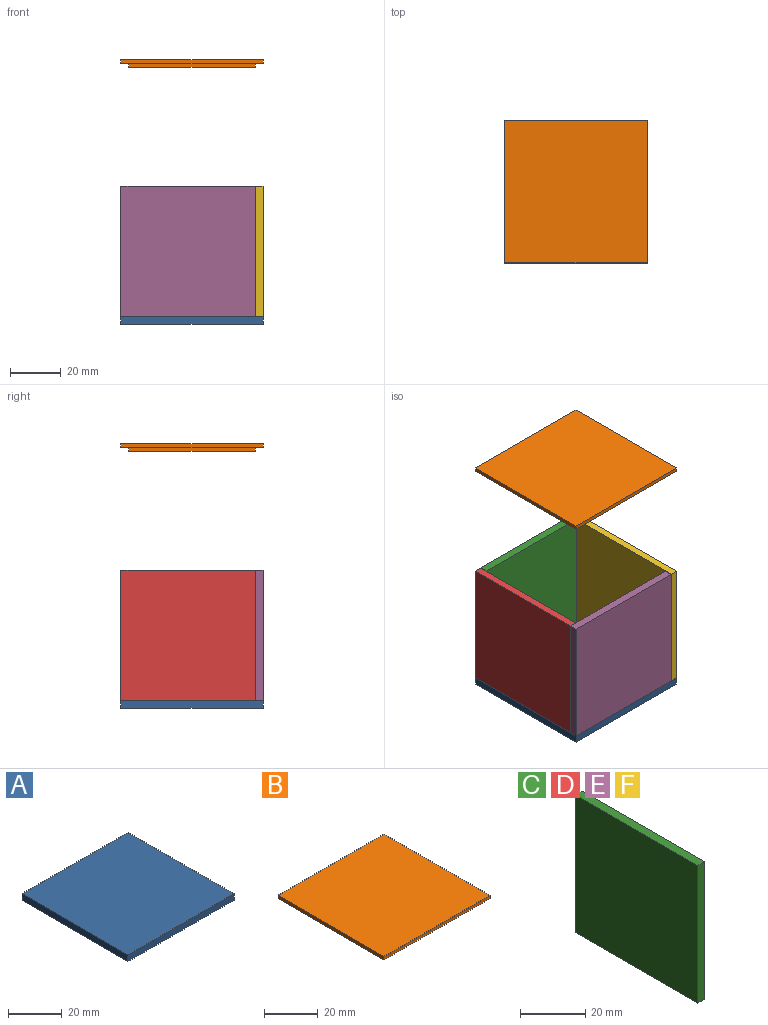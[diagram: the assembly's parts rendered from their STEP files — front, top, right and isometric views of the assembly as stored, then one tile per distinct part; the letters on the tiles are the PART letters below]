
ASSEMBLY  parts=6 mates=14
PART A: 6 faces, bbox 56x56x3 mm
  f0: plane 56x3mm, normal (0,1,0), area 168mm2, adj f1,f3,f4,f5
  f1: plane 56x3mm, normal (-1,0,0), area 168mm2, adj f0,f2,f4,f5
  f2: plane 56x3mm, normal (0,-1,0), area 168mm2, adj f1,f3,f4,f5
  f3: plane 56x3mm, normal (1,0,0), area 168mm2, adj f0,f2,f4,f5
  f4: plane 56x56mm, normal (0,0,1), area 3136mm2, adj f0,f1,f2,f3
  f5: plane 56x56mm, normal (0,0,-1), area 3136mm2, adj f0,f1,f2,f3
PART B: 11 faces, bbox 56x56x3 mm
  f0: plane 56x1.5mm, normal (0,1,0), area 84mm2, adj f1,f3,f4,f9
  f1: plane 56x1.5mm, normal (-1,0,0), area 84mm2, adj f0,f2,f4,f9
  f2: plane 56x1.5mm, normal (0,-1,0), area 84mm2, adj f1,f3,f4,f9
  f3: plane 56x1.5mm, normal (1,0,0), area 84mm2, adj f0,f2,f4,f9
  f4: plane 56x56mm, normal (0,0,1), area 3136mm2, adj f0,f1,f2,f3
  f5: plane 50x1.5mm, normal (1,0,0), area 75mm2, adj f6,f8,f9,f10
  f6: plane 50x1.5mm, normal (0,1,0), area 75mm2, adj f5,f7,f9,f10
  f7: plane 50x1.5mm, normal (-1,0,0), area 75mm2, adj f6,f8,f9,f10
  f8: plane 50x1.5mm, normal (0,-1,0), area 75mm2, adj f5,f7,f9,f10
  f9: plane 56x56mm, normal (0,0,-1), area 636mm2, adj f0,f1,f2,f3,f5,f6,f7,f8
  f10: plane 50x50mm, normal (0,0,-1), area 2500mm2, adj f5,f6,f7,f8
PART C: 6 faces, bbox 3x53x51.5 mm
  f0: plane 51.5x3mm, normal (0,-1,0), area 154.5mm2, adj f1,f3,f4,f5
  f1: plane 53x3mm, normal (0,0,-1), area 159mm2, adj f0,f2,f4,f5
  f2: plane 51.5x3mm, normal (0,1,0), area 154.5mm2, adj f1,f3,f4,f5
  f3: plane 53x3mm, normal (0,0,1), area 159mm2, adj f0,f2,f4,f5
  f4: plane 53x51.5mm, normal (1,0,0), area 2729.5mm2, adj f0,f1,f2,f3
  f5: plane 53x51.5mm, normal (-1,0,0), area 2729.5mm2, adj f0,f1,f2,f3
PART D: same geometry as C
PART E: same geometry as C
PART F: same geometry as C
PLACE A t=(-9.22,69.67,-13.62)mm
PLACE B t=(-9.22,69.67,87.68)mm
PLACE C rot(axis=(0,0,-1),90deg) t=(-34.22,97.67,-10.62)mm
PLACE D t=(-37.22,44.67,-10.62)mm
PLACE E rot(axis=(0.71,-0.71,0),180deg) t=(15.78,44.67,40.88)mm
PLACE F t=(15.78,41.67,-10.62)mm
MATE planar A.f4 <-> F.f1  axis (0,0,1) through (-9.22,69.67,-10.62)mm
MATE planar F.f0 <-> A.f2  axis (0,-1,0) through (17.28,41.67,15.13)mm
MATE planar D.f1 <-> A.f4  axis (0,0,-1) through (-35.72,71.17,-10.62)mm
MATE planar D.f2 <-> C.f5  axis (0,1,0) through (-35.72,97.67,15.13)mm
MATE planar C.f2 <-> F.f4  axis (1,0,0) through (18.78,96.17,15.13)mm
MATE planar C.f5 <-> A.f0  axis (0,1,0) through (-7.72,97.67,15.13)mm
MATE planar C.f1 <-> A.f4  axis (0,0,-1) through (-7.72,96.17,-10.62)mm
MATE planar B.f1 <-> D.f5  axis (-1,0,0) through (-37.22,69.67,89.93)mm
MATE planar D.f5 <-> A.f1  axis (-1,0,0) through (-37.22,71.17,15.13)mm
MATE planar E.f2 <-> D.f5  axis (-1,0,0) through (-37.22,43.17,15.13)mm
MATE planar F.f4 <-> A.f3  axis (1,0,0) through (18.78,68.17,15.13)mm
MATE planar B.f2 <-> E.f4  axis (0,-1,0) through (-9.22,41.67,89.93)mm
MATE planar E.f3 <-> A.f4  axis (0,0,-1) through (-10.72,43.17,-10.62)mm
MATE planar E.f4 <-> A.f2  axis (0,-1,0) through (-10.72,41.67,15.13)mm
